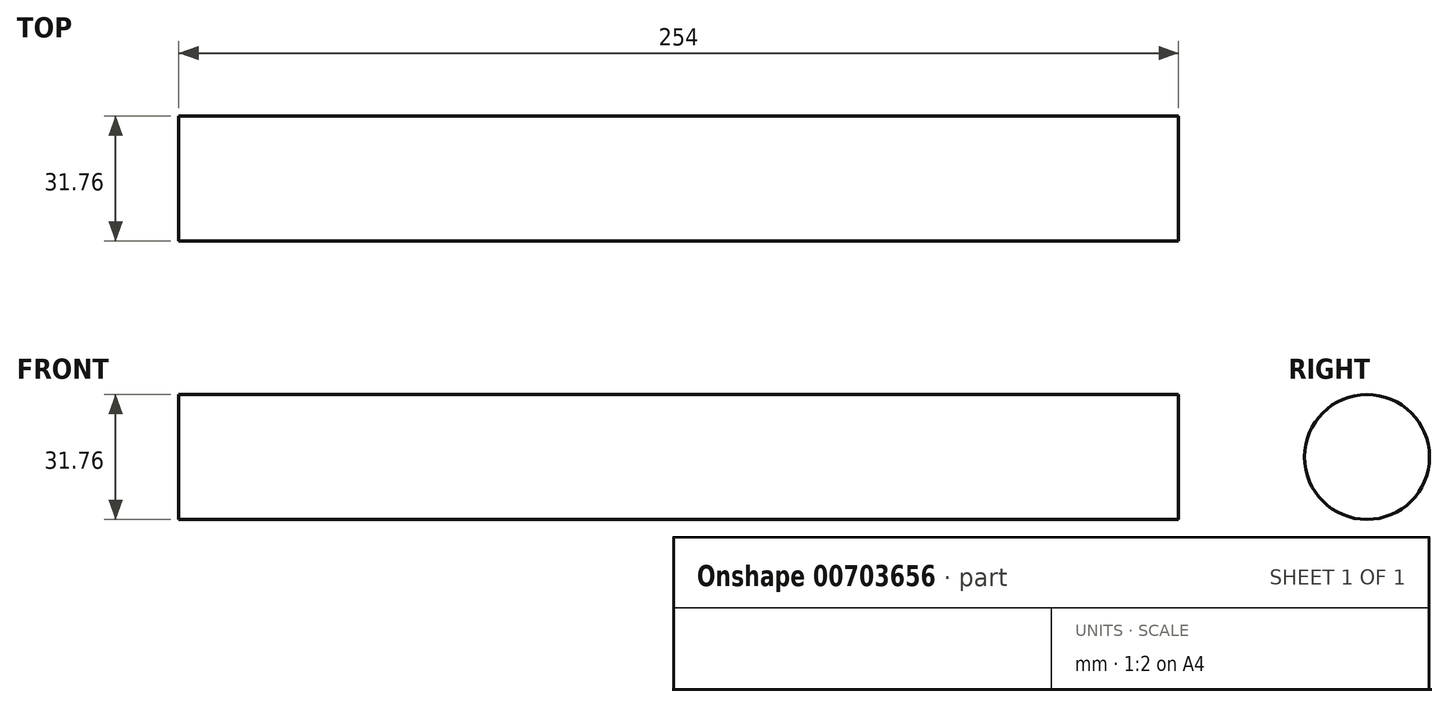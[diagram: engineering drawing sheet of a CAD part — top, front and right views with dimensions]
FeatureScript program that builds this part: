
annotation { "Feature Type Name" : "Feature", "Feature Type Description" : "" }
export const myFeature = defineFeature(function(context is Context, id is Id, definition is map)
    precondition{}
    {
        {
            var Q0;
            Q0=qCreatedBy(makeId("Right.planeOp"),FACE);
            var sketch = newSketch(context, id + "F0", { "sketchPlane" : qUnion([Q0])});
            skCircle(sketch, "E0", {"center": v(0, 0) * mm, "radius": 15.88 * mm});
            skSolve(sketch);
        }
        {
            var Q0;
            Q0=makeQuery(id+"F0.imprint","IMPRINT",FACE,{"disambiguationData":[TD([[makeQuery(id+"F0.imprint","IMPRINT",EDGE,{"derivedFrom":sQuery(id+"F0.wireOp",EDGE,"E0")}),1.0]])]});
            extrude(context, id + "F1", {"entities" : qUnion([Q0]), "depth" : 254 * mm, "offsetDistance" : 25.4 * mm});
        }
    });
